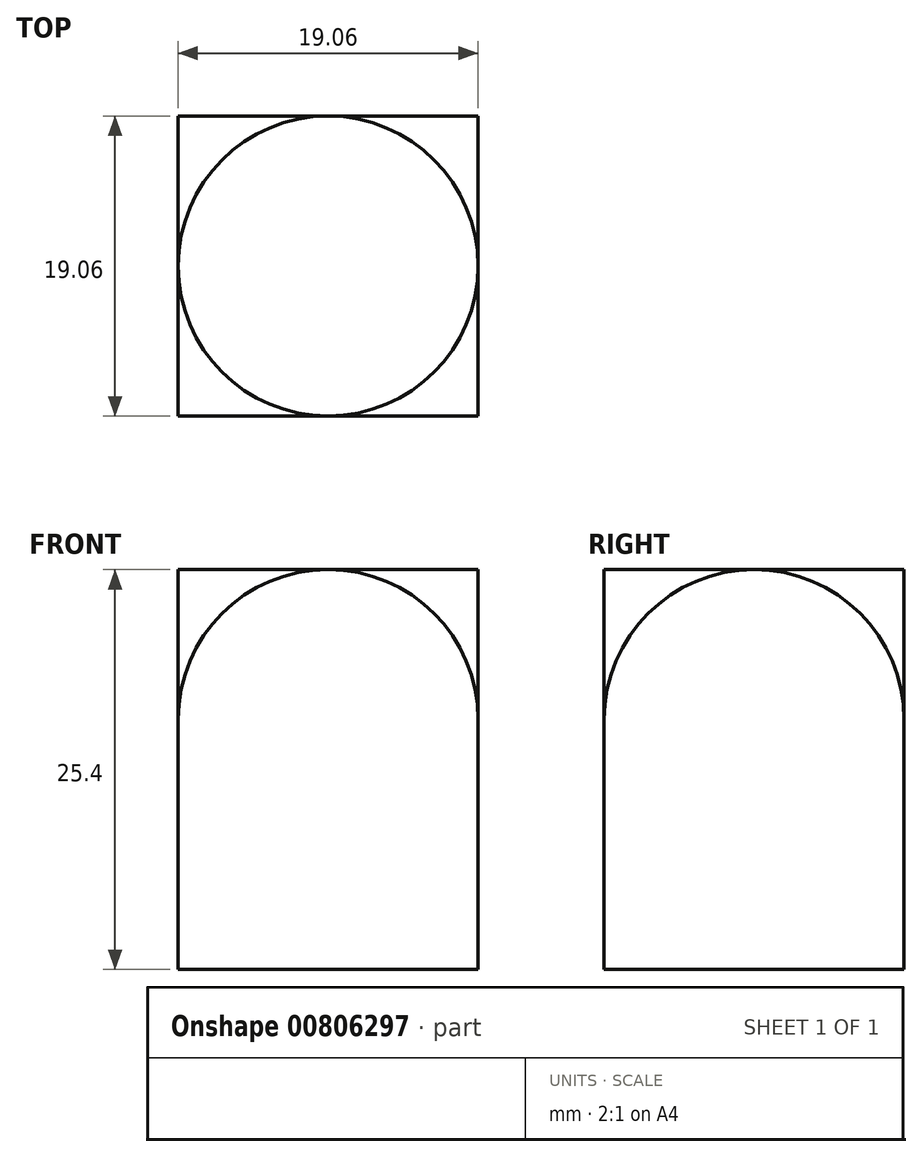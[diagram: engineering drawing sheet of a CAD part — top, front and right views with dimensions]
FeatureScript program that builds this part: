
annotation { "Feature Type Name" : "Feature", "Feature Type Description" : "" }
export const myFeature = defineFeature(function(context is Context, id is Id, definition is map)
    precondition{}
    {
        {
            var Q0;
            Q0=qCreatedBy(makeId("Top.planeOp"),FACE);
            var sketch = newSketch(context, id + "F0", { "sketchPlane" : qUnion([Q0])});
            skLineSegment(sketch, "E0.bottom", {"start": v(-9.52, -9.53) * mm, "end": v(9.53, -9.53) * mm});
            skLineSegment(sketch, "E0.top", {"start": v(-9.53, 9.52) * mm, "end": v(9.52, 9.52) * mm});
            skLineSegment(sketch, "E0.left", {"start": v(-9.52, -9.53) * mm, "end": v(-9.53, 9.52) * mm});
            skLineSegment(sketch, "E0.right", {"start": v(9.53, -9.53) * mm, "end": v(9.52, 9.52) * mm});
            skPoint(sketch, "E0.middle", {"position": v(0, 0) * mm});
            skSolve(sketch);
        }
        {
            var Q0;
            Q0=makeQuery(id+"F0.imprint","IMPRINT",FACE,{"disambiguationData":[TD([[makeQuery(id+"F0.imprint","IMPRINT",EDGE,{"derivedFrom":sQuery(id+"F0.wireOp",EDGE,"E0.bottom")}),1.0]])]});
            extrude(context, id + "F1", {"entities" : qUnion([Q0]), "oppositeDirection" : true, "depth" : 25.4 * mm, "offsetDistance" : 25.4 * mm});
        }
        {
            var Q0;
            Q0=makeQuery(id+"F1.opExtrude","CAP_VERTEX",VERTEX,{"disambiguationData":[OSD([sQuery(id+"F0.wireOp",EDGE,"E0.bottom"),sQuery(id+"F0.wireOp",EDGE,"E0.left")])],"isStart":false});
            var Q1;
            Q1=makeQuery(id+"F1.opExtrude","CAP_VERTEX",VERTEX,{"disambiguationData":[OSD([sQuery(id+"F0.wireOp",EDGE,"E0.bottom"),sQuery(id+"F0.wireOp",EDGE,"E0.left")])],"isStart":true});
            var Q2;
            Q2=makeQuery(id+"F1.opExtrude","CAP_VERTEX",VERTEX,{"disambiguationData":[OSD([sQuery(id+"F0.wireOp",EDGE,"E0.top"),sQuery(id+"F0.wireOp",EDGE,"E0.right")])],"isStart":true});
            cPlane(context, id + "F2", {"entities" : qUnion([Q0, Q1, Q2]), "cplaneType" : CPlaneType.THREE_POINT, "offset" : 25.4 * mm, "width" : 152.4 * mm, "height" : 152.4 * mm});
        }
        {
            var Q0;
            Q0=qCreatedBy(id+"F2.planeOp",FACE);
            var sketch = newSketch(context, id + "F3", { "sketchPlane" : qUnion([Q0])});
            skPoint(sketch, "E1", {"position": v(0, -9.52) * mm});
            skArc(sketch, "E2", {"start": v(13.47, -9.52) * mm, "mid": v(9.52, 0) * mm, "end": v(0, 3.95) * mm});
            skLineSegment(sketch, "E3", {"start": v(0, 3.95) * mm, "end": v(0, -21.46) * mm, "construction": true});
            skLineSegment(sketch, "E4.0", {"start": v(16.01, 6.49) * mm, "end": v(16.01, -9.52) * mm});
            skLineSegment(sketch, "E4.1", {"start": v(0, 6.49) * mm, "end": v(16.01, 6.49) * mm});
            skLineSegment(sketch, "E5", {"start": v(13.47, -9.52) * mm, "end": v(16.01, -9.52) * mm});
            skLineSegment(sketch, "E6", {"start": v(0, 6.49) * mm, "end": v(0, 3.95) * mm});
            skPoint(sketch, "E7", {"position": v(9.53, 0) * mm});
            skSolve(sketch);
        }
        {
            var Q0;
            Q0=makeQuery(id+"F3.imprint","IMPRINT",FACE,{"disambiguationData":[TD([[makeQuery(id+"F3.imprint","IMPRINT",EDGE,{"derivedFrom":sQuery(id+"F3.wireOp",EDGE,"E2")}),-1.0]])]});
            var Q1;
            Q1=sQuery(id+"F3.wireOp",EDGE,"E3");
            revolve(context, id + "F4", {"operationType" : NewBodyOperationType.REMOVE, "surfaceOperationType" : NewSurfaceOperationType.NEW, "entities" : qUnion([Q0]), "axis" : qUnion([Q1]), "revolveType" : RevolveType.FULL, "oppositeDirection" : true});
        }
    });
